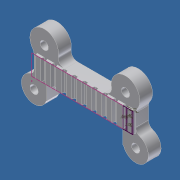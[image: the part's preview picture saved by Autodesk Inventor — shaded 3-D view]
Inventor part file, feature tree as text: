
AUTODESK INVENTOR PART (.ipt)
format: ipt  version: unknown  size: 350,208 bytes
history: native  units: in
note: dims shown in document units (in); Inventor stores cm internally (conversion verified against a paired STEP export)
features: fillet x6, sketch x5, extrude x4
ambient origin geometry x8: Origin, YZ Plane, XZ Plane, XY Plane, X Axis, Y Axis, Z Axis, Center Point
bodies: Solid1 (feature_tree)
feature tree (15):
  extrude  "Extrusion1"  Depth=0.16in
  fillet  "Fillet1"  Radius=0.4in
  fillet  "Fillet2"  Radius=2.0in
  fillet  "Fillet3"  Radius=0.25in
  fillet  "Fillet4"  Radius=0.125in
  fillet  "Fillet5"  Radius=0.125in
  fillet  "Fillet6"  Radius=0.125in
  extrude  "Extrusion2"  Depth=0.125in
  sketch  "Sketch3"  dims[d40=0.125in d43=2.0in]
  extrude  "Extrusion3"  Depth=2.0in
  extrude  "Extrusion4"  Depth=0.14in
  sketch  "Sketch1"  dims[d28=0.4693in d29=0.16in d30=0.4in d31=2.0in d33=0.25in d34=0.0in d35=0.125in d36=0.125in d37=0.125in]
  sketch  "Sketch2"  dims[d38=0.125in d39=0.125in]
  sketch  "Sketch4"  dims[d69=0.049in d70=0.0in d71=0.14in]
  sketch  "Sketch5"  dims[d72=0.06in d73=0.02in d74=0.1in d75=0.02in d76=1.0in d77=0.0in d78=0.14in d80=0.06in d82=0.06in d83=0.06in d84=0.06in d85=0.06in d86=0.06in d87=0.06in d88=0.06in d89=0.06in d90=0.06in d91=1.0in d92=0.0in d100=1.5in]
